# Revit family: CANGINITUCCI_LIGHTING_FIXTURE_PIT_GROUP
name_source: partatom
category: Lighting Fixtures
units: mm (PartAtom-declared; Revit-internal decimal feet)

## family parameters
Cut with Voids When Loaded = No
Host = Face
Light Source = No
Part Type = Normal
Room Calculation Point = Yes
Round Connector Dimension = Use Diameter
Shared = No

## types (1)
- CANGINITUCCI_LIGHTING_FIXTURE_PIT_GROUP
    BIM BADGE = https://bim.archiproducts.com
    COLLECTION = PIT
    DIAMETER = 430 mm
    Default Elevation = 1219 mm
    Description = PIT is a family of LED lamps handcrafted in blown glass.‎ The family consists of 3 types: the hanging lamp, made in 4 different diameters, the table lamp with a 22cm diameter sphere and a height of 50cm, and the floor lamp, with a 30cm diameter sphere and a height of 175cm.‎
    ENERGY EFFICIENCY CLASS = A
    FINISHING MATERIAL = CANGINITUCCI_GLASS
    HEIGHT = 1000 mm
    LAMP MATERIAL = CANGINITUCCI_LIGHT
    Manufacturer = CANGINI&TUCCI
    Model = GLASS LAMP - TRIPLE
    POWER SUPPLY = REFER TO SINGLE LAMP SPEC
    PRODUCT CODE = 1589MX.43.3L
    PRODUCT SHEET = https://www.archiproducts.com
    STRUCTURE MATERIAL = CANGINITUCCI_METAL
    TECHNICAL SHEET = https://www.canginietucci.com
    URL = https://www.canginietucci.com
    WEIGHT = 0.00 kg

## geometry (parser evidence)
native form markers: Blend x6, Sweep x4
no freeform markers — native parametric forms only
